# Revit family: DEVIreg Solo_RFA_1
name_source: partatom
category: Data Devices
units: mm (PartAtom-declared; Revit-internal decimal feet)

## family parameters
Cut with Voids When Loaded = No
Host = Face
Maintain Annotation Orientation = No
OmniClass Number = 23.85.50.17
OmniClass Title = Communication and Data Processing Equipment
Part Type = Normal
Room Calculation Point = No
Round Connector Dimension = Use Diameter
Shared = No

## types (2) — shared parameters
Ambient Temperature Range = 0 °C to 35 °C
Ball pressure test temperature = 75 °C
Cable specification for connector terminals, max. = 1 x 4 mm² or 2 x 2.5 mm²
Controller type = 1 B
D = 10 mm  [stored 0.0328084 ft]
Description = Programmable timer thermostat
Frost protection = 4 °C to 9 °C (default 5 °C )
H = 85 mm  [stored 0.278871 ft]
IP Rating = 21
IfcExportAs = IfcElectricApplianceType
IfcExportType = DEVIreg Solo
In wall depth = 23 mm  [stored 0.0754593 ft]
Inductive load = Cos Φ = 0.3 max. 1A
L = 10 mm  [stored 0.0328084 ft]
LOD 200 = No
LOD 350 = Yes
Manufacturer = Danfoss
Mounting method = In-wall
NominalHeight = 85 mm  [stored 0.278871 ft]
NominalLength = 10 mm  [stored 0.0328084 ft]
NominalWidth = 85 mm  [stored 0.278871 ft]
Operating Temperature Range = 0 °C to 35 °C, 90% RH non-condensing
Pollution degree = 2 (domestic use)
Power = 1 W
Protection class = Class II
Regulation = PWM - Pulse Width Modulation
Resistive load = 16A / 3680W @ 230V
Sensing unit = NTC 15 kΩ @ 25 °C, 3 m. (default),
NTC 10 kΩ @ 25 °C,
NTC 6.8 kΩ @ 25 °C,
NTC 33 kΩ @ 25 °C,
NTC 12 kΩ @ 25 °C,
NTC 47 kΩ @ 25 °C
Software class = A
Standby power consumption = 1 W
Storage temperature = -25 °C to 60 °C, 90% RH non-condensing
URL = https://store.danfoss.com
Voltage = 230 V
W = 85 mm  [stored 0.278871 ft]
Weight = 0.11 kg
r1 = 1 mm  [stored 0.00328084 ft]
r2 = 1 mm  [stored 0.00328084 ft]
w2 = 56 mm  [stored 0.183727 ft]
w2_1 = 56 mm  [stored 0.183727 ft]
w3 = 82 mm  [stored 0.269029 ft]
zero-valued in all types: Default Elevation

## per-type parameters (varying)
| type | Body Material | Model | Model Type |
| DEVIreg™ Solo (White)_140F1172 | Danfoss Plastic White | 140F1172 | DEVIreg™ Solo (White) |
| DEVIreg™ Solo (Black)_140F1173 | Danfoss Plastic Black | 140F1173 | DEVIreg™ Solo (Black) |

note: [stored X ft] marks values corroborated as IEEE doubles in the binary element streams (Revit-internal decimal feet)

## geometry (parser evidence)
native form markers: Sweep x2
no freeform markers — native parametric forms only
